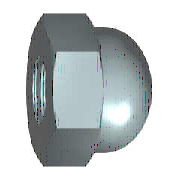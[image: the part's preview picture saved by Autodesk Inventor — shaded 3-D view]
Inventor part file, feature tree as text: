
AUTODESK INVENTOR PART (.ipt)
format: ipt  version: 2018 (Build 220112000, 112)  size: 210,432 bytes
history: native  units: mm (DEFAULTED — no unit token found)
features: sketch x4, other x3, extrude x1, hole x1, plane x1
ambient origin geometry x7: Origin, YZ Plane, XZ Plane, X Axis, Y Axis, Z Axis, Center Point
bodies: Solid1 (feature_tree)
feature tree (10):
  extrude  "Corpo"  Depth=15.011107mm
  other  "Calotta"
  hole  "Filettatura"  [1 undecoded]
  other  "Smusso1"
  other  "Work Axis1"
  plane  "Work Plane1"
  sketch  "Schizzo1"
  sketch  "Schizzo4"
  sketch  "Schizzo2"
  sketch  "Schizzo3"
note: 1 required parameter value undecoded (feature->parameter linkage not recoverable at this tier; creation-order binding heuristic only, values carry confidence <= 0.55)
